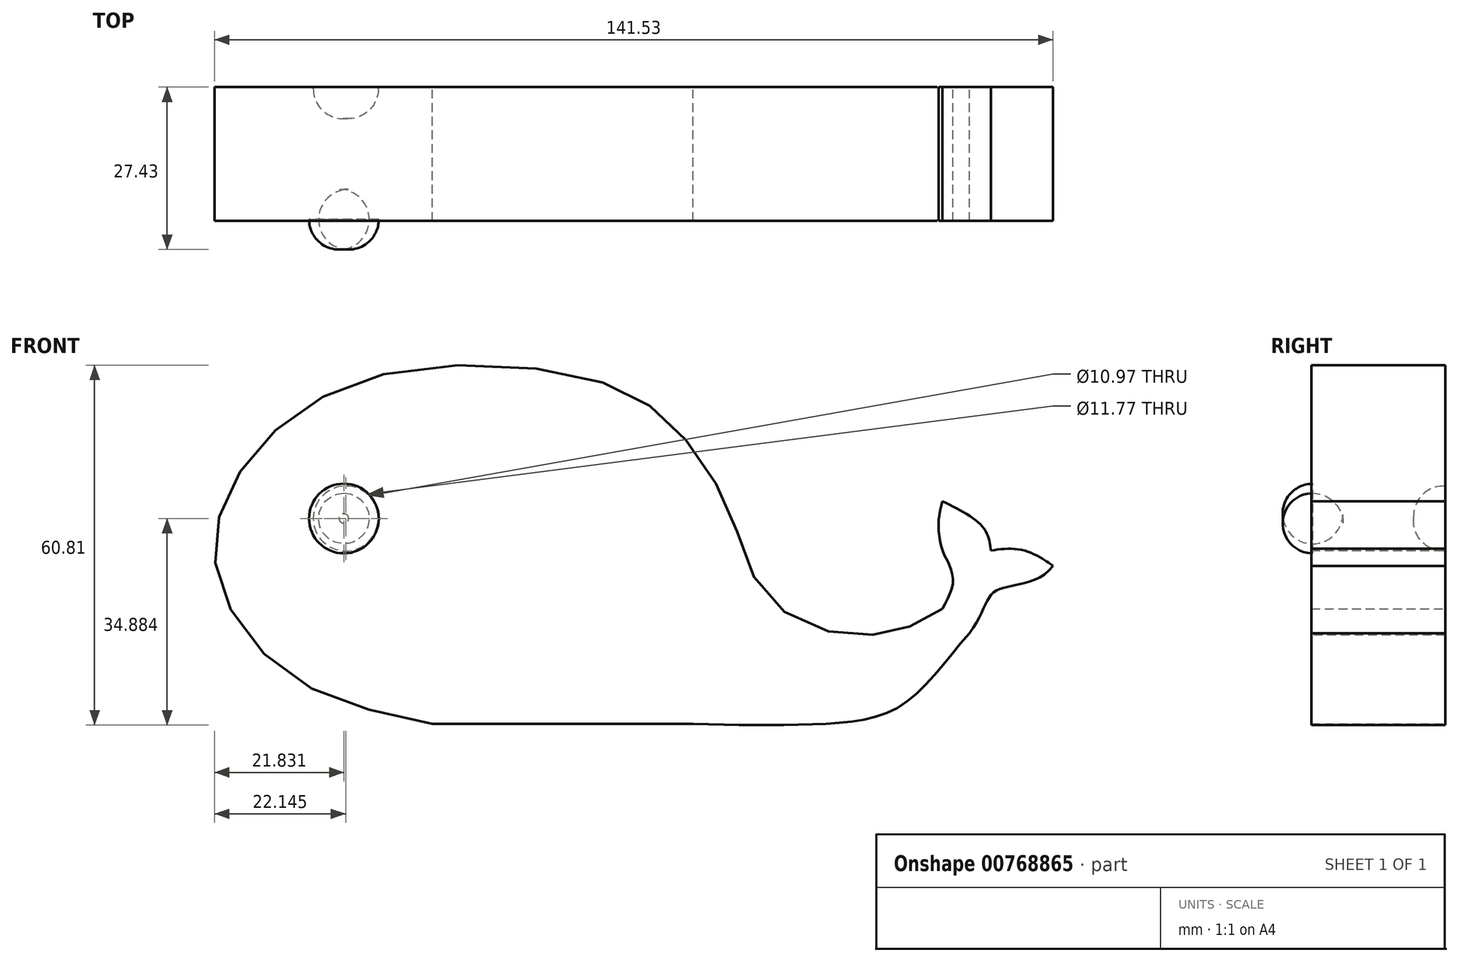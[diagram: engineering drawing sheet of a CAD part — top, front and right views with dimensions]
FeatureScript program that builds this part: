
annotation { "Feature Type Name" : "Feature", "Feature Type Description" : "" }
export const myFeature = defineFeature(function(context is Context, id is Id, definition is map)
    precondition{}
    {
        {
            var Q0;
            Q0=qCreatedBy(makeId("Front.planeOp"),FACE);
            var sketch = newSketch(context, id + "F0", { "sketchPlane" : qUnion([Q0])});
            skLineSegment(sketch, "E0", {"start": v(-21.39, 0) * mm, "end": v(22.59, 0) * mm});
            skFitSpline(sketch, "E1", {"points": [v(-21.39, 0) * mm, v(-44.18, 7.4) * mm, v(-56.57, 21.79) * mm, v(-57.37, 34.98) * mm, v(-48.58, 48.98) * mm, v(-28.19, 59.37) * mm, v(5.8, 58.17) * mm, v(19.8, 49.78) * mm, v(28.99, 35.38) * mm, v(34.58, 22.19) * mm, v(46.58, 15.4) * mm, v(57.29, 15.88) * mm, v(64.7, 19.43) * mm], "startDerivative": vector(-256.25, 52.79) * mm, "endDerivative": vector(136.72, 97.08) * mm});
            skFitSpline(sketch, "E2", {"points": [v(64.7, 37.63) * mm, v(71.62, 33.17) * mm, v(72.91, 29.3) * mm], "startDerivative": vector(13.96, -6.74) * mm, "endDerivative": vector(1.33, -9.68) * mm});
            skFitSpline(sketch, "E3", {"points": [v(72.91, 29.3) * mm, v(78.6, 29.3) * mm, v(82.49, 27.35) * mm, v(83.38, 26.72) * mm], "startDerivative": vector(12.76, 2.44) * mm, "endDerivative": vector(1.77, -1.28) * mm});
            skFitSpline(sketch, "E4", {"points": [v(83.38, 26.72) * mm, v(73.8, 22.53) * mm, v(69.28, 15.36) * mm], "startDerivative": vector(-15.2, -20.39) * mm, "endDerivative": vector(-16.97, -21.66) * mm});
            skFitSpline(sketch, "E5", {"points": [v(22.59, 0) * mm, v(43.98, 0) * mm, v(57.92, 3.23) * mm, v(69.28, 15.36) * mm], "startDerivative": vector(60.46, -1.45) * mm, "endDerivative": vector(35.71, 39.86) * mm});
            skFitSpline(sketch, "E6", {"points": [v(64.7, 37.63) * mm, v(64.08, 33.87) * mm, v(64.7, 29.48) * mm, v(65.79, 27.06) * mm, v(66.49, 23.91) * mm, v(64.7, 19.43) * mm], "startDerivative": vector(-4.35, -17.74) * mm, "endDerivative": vector(-11.04, -20.22) * mm});
            skSolve(sketch);
        }
        {
            var Q0;
            Q0=qCreatedBy(makeId("Front.planeOp"),FACE);
            var sketch = newSketch(context, id + "F1", { "sketchPlane" : qUnion([Q0])});
            skCircle(sketch, "E7", {"center": v(-36, 34.71) * mm, "radius": 5.49 * mm});
            skSolve(sketch);
        }
        {
            var Q0;
            Q0 = qSketchRegion(id + "F0", true);
            extrude(context, id + "F2", {"entities" : qUnion([Q0]), "depth" : 22.6 * mm, "offsetDistance" : 25.4 * mm});
        }
        {
            var Q0;
            Q0 = qSketchRegion(id + "F1", true);
            extrude(context, id + "F3", {"entities" : qUnion([Q0]), "operationType" : NewBodyOperationType.REMOVE, "depth" : 5.33 * mm, "offsetDistance" : 25.4 * mm});
        }
        {
            var Q0;
            Q0=makeQuery(id+"F2.opExtrude","CAP_FACE",FACE,{"disambiguationData":[OSD([sQuery(id+"F0.wireOp",EDGE,"E0"),sQuery(id+"F0.wireOp",EDGE,"E1"),sQuery(id+"F0.wireOp",EDGE,"E2"),sQuery(id+"F0.wireOp",EDGE,"E3"),sQuery(id+"F0.wireOp",EDGE,"E4"),sQuery(id+"F0.wireOp",EDGE,"E5"),sQuery(id+"F0.wireOp",EDGE,"E6")])],"isStart":false});
            var sketch = newSketch(context, id + "F4", { "sketchPlane" : qUnion([Q0])});
            skCircle(sketch, "E8", {"center": v(-36.32, 34.71) * mm, "radius": 5.89 * mm});
            skSolve(sketch);
        }
        {
            var Q0;
            Q0=makeQuery(id+"F4.imprint","IMPRINT",FACE,{"disambiguationData":[TD([[makeQuery(id+"F4.imprint","IMPRINT",EDGE,{"derivedFrom":sQuery(id+"F4.wireOp",EDGE,"E8")}),1.0]])]});
            extrude(context, id + "F5", {"entities" : qUnion([Q0]), "operationType" : NewBodyOperationType.REMOVE, "oppositeDirection" : true, "depth" : 5.33 * mm, "offsetDistance" : 25.4 * mm});
        }
        {
            var Q0;
            Q0=makeQuery(id+"F5.boolean.opBoolean","COPY",EDGE,{"derivedFrom":makeQuery(id+"F5.opExtrude","CAP_EDGE",EDGE,{"disambiguationData":[OSD([sQuery(id+"F4.wireOp",EDGE,"E8")])],"isStart":false})});
            var Q1;
            Q1=makeQuery(id+"F3.boolean.opBoolean","COPY",EDGE,{"derivedFrom":makeQuery(id+"F3.opExtrude","CAP_EDGE",EDGE,{"disambiguationData":[OSD([sQuery(id+"F1.wireOp",EDGE,"E7")])],"isStart":false})});
            fillet(context, id + "F6", {"entities" : qUnion([Q0, Q1]), "radius" : 5.08 * mm, "tangentPropagation" : true, "allowEdgeOverflow" : false});
        }
    });
